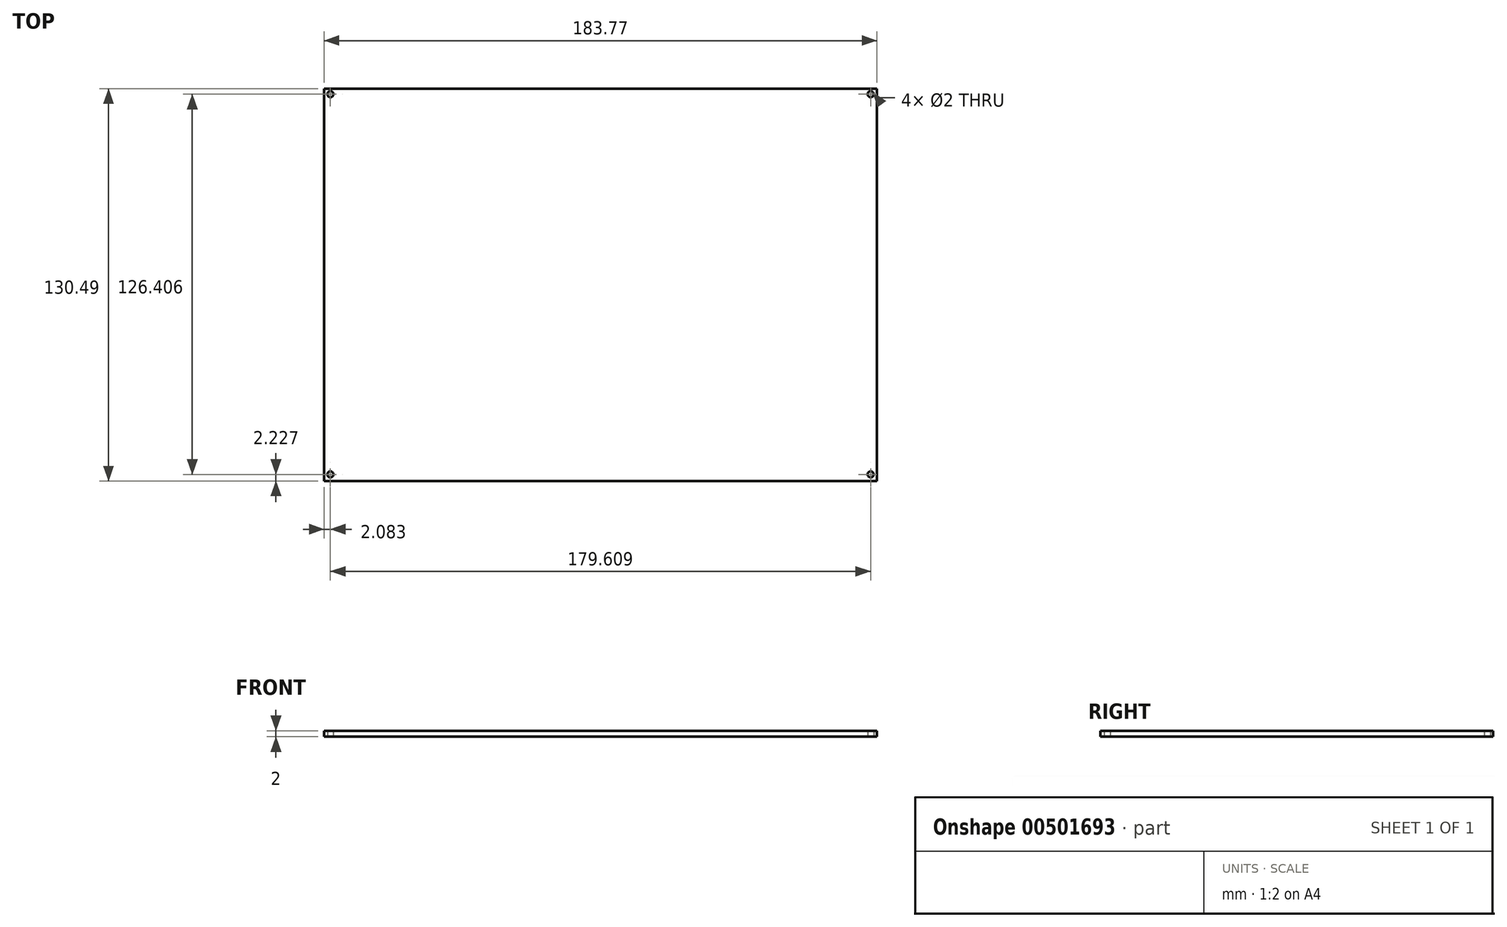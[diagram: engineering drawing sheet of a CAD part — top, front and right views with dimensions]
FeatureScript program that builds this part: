
annotation { "Feature Type Name" : "Feature", "Feature Type Description" : "" }
export const myFeature = defineFeature(function(context is Context, id is Id, definition is map)
    precondition{}
    {
        {
            var Q0;
            Q0=qCreatedBy(makeId("Top.planeOp"),FACE);
            var sketch = newSketch(context, id + "F0", { "sketchPlane" : qUnion([Q0])});
            skLineSegment(sketch, "E0.bottom", {"start": v(-49.2, -18.06) * mm, "end": v(-29.2, -18.06) * mm});
            skLineSegment(sketch, "E0.top", {"start": v(-49.2, -47.06) * mm, "end": v(-29.2, -47.06) * mm});
            skLineSegment(sketch, "E0.left", {"start": v(-49.2, -18.06) * mm, "end": v(-49.2, -47.06) * mm});
            skLineSegment(sketch, "E0.right", {"start": v(-29.2, -18.06) * mm, "end": v(-29.2, -47.06) * mm});
            skLineSegment(sketch, "E1", {"start": v(-39.2, -18.06) * mm, "end": v(-39.2, -13.06) * mm});
            skLineSegment(sketch, "E2", {"start": v(-39.2, -13.06) * mm, "end": v(-49.2, -18.06) * mm});
            skLineSegment(sketch, "E3", {"start": v(-39.2, -13.06) * mm, "end": v(-29.2, -18.06) * mm});
            skLineSegment(sketch, "E4", {"start": v(-39.2, -13.06) * mm, "end": v(-39.2, -15.56) * mm});
            skCircle(sketch, "E5", {"center": v(-39.2, -15.56) * mm, "radius": 1 * mm});
            skLineSegment(sketch, "E6", {"start": v(-39.2, -47.06) * mm, "end": v(-39.2, -52.06) * mm});
            skLineSegment(sketch, "E7", {"start": v(-39.2, -52.06) * mm, "end": v(-29.2, -47.06) * mm});
            skLineSegment(sketch, "E8", {"start": v(-39.2, -52.06) * mm, "end": v(-49.2, -47.06) * mm});
            skLineSegment(sketch, "E9", {"start": v(-39.2, -52.06) * mm, "end": v(-39.2, -50.06) * mm});
            skCircle(sketch, "E10", {"center": v(-39.2, -50.06) * mm, "radius": 1 * mm});
            skSolve(sketch);
        }
        {
            var Q0;
            Q0=qCreatedBy(makeId("Top.planeOp"),FACE);
            var sketch = newSketch(context, id + "F1", { "sketchPlane" : qUnion([Q0])});
            skLineSegment(sketch, "E11.bottom", {"start": v(-51.47, 131.97) * mm, "end": v(132.3, 131.97) * mm});
            skLineSegment(sketch, "E11.top", {"start": v(-51.47, 1.48) * mm, "end": v(132.3, 1.48) * mm});
            skLineSegment(sketch, "E11.left", {"start": v(-51.47, 131.97) * mm, "end": v(-51.47, 1.48) * mm});
            skLineSegment(sketch, "E11.right", {"start": v(132.3, 131.97) * mm, "end": v(132.3, 1.48) * mm});
            skCircle(sketch, "E12", {"center": v(-49.39, 130.11) * mm, "radius": 1 * mm});
            skCircle(sketch, "E13", {"center": v(130.22, 130.11) * mm, "radius": 1 * mm});
            skCircle(sketch, "E14", {"center": v(130.22, 3.7) * mm, "radius": 1 * mm});
            skCircle(sketch, "E15", {"center": v(-49.39, 3.7) * mm, "radius": 1 * mm});
            skSolve(sketch);
        }
        {
            var Q0;
            Q0=makeQuery(id+"F1.imprint","IMPRINT",FACE,{"disambiguationData":[TD([[makeQuery(id+"F1.imprint","IMPRINT",EDGE,{"derivedFrom":sQuery(id+"F1.wireOp",EDGE,"E11.bottom")}),-1.0]])]});
            extrude(context, id + "F2", {"entities" : qUnion([Q0]), "depth" : 2 * mm, "offsetDistance" : 25 * mm});
        }
    });
